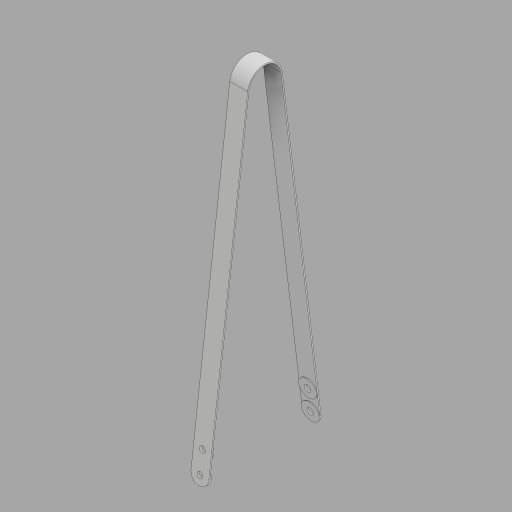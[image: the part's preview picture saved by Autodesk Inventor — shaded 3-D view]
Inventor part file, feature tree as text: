
AUTODESK INVENTOR PART (.ipt)
format: ipt  version: 2023 (Build 270158000, 158)  size: 159,744 bytes
history: native  units: mm
features: extrude x7, sketch x3
ambient origin geometry x8: Origin, YZ Plane, XZ Plane, XY Plane, X Axis, Y Axis, Z Axis, Center Point
bodies: Solid1 (feature_tree)
feature tree (10):
  extrude  "Extrusion1"  Depth=254.37mm
  sketch  "Sketch2"  dims[d2=180.0deg d3=35.0mm]
  extrude  "Extrusion2"  Depth=35.0mm
  extrude  "Extrusion3"  Depth=1.0mm
  extrude  "Extrusion4"  Depth=1.0mm
  sketch  "Sketch3"  dims[d4=100.0mm d5=2.0mm d6=1.0mm d7=1.0mm d8=15.0mm d9=0.0mm d10=15.0mm d11=15.0mm d12=2.5mm d13=15.0mm d14=15.0mm d15=1.0mm d16=0.0mm d17=2.0mm d18=0.0mm d19=2.0mm d20=0.0mm d21=15.0mm d22=15.0mm d23=2.5mm d24=15.0mm d25=1.0mm d26=0.0mm d27=5.5mm d28=5.5mm d29=2.0mm d30=0.0mm d31=2.0mm d32=0.0mm]
  extrude  "Extrusion5"  Depth=1.0mm
  extrude  "Extrusion6"  Depth=15.0mm TaperAngle=0.0deg
  extrude  "Extrusion7"  Depth=15.0mm
  sketch  "Sketch1"  dims[d0=29.224mm d1=254.37mm]
